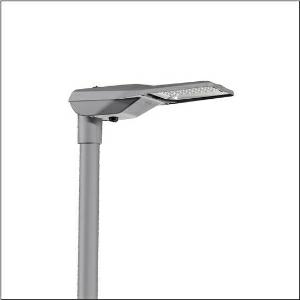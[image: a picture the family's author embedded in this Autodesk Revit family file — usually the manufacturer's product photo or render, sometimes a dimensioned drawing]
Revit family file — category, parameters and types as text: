
# Revit family: streetlight_sl_21_mini___p0_5a_5xe2v33t08gb_dcd0
name_source: partatom
category: Lighting Fixtures
units: mm (PartAtom-declared; Revit-internal decimal feet)

## family parameters
Cut with Voids When Loaded = No
Host = Face
Light Source = No
Part Type = Normal
Room Calculation Point = No
Round Connector Dimension = Use Diameter
Shared = No

## types (1)
- --- (1 x LED, 5840 lm, 40.4 W, 3000K)
    Apparent Load = 40 VA
    CIE Flux Codes = 37 73 96 100 100
    Color Rendering = 70
    Color Temperature = 3000K
    Default Elevation = 1800 mm
    Description = Streetlight SL 21 mini, mast luminaire, primary light control with lens, of PMMA, primary optical cover: cover, of toughened safety glass, transparent, light distribution: P0.5a, light emission: direct distribution, primary light characteristic: asymmetric, installation type: post-top, side-entry, LED, High Power LED, rated luminous flux: 5.840lm, luminous efficacy: 145lm/W, light colour: 730, colour temperature: 3000K, control gear: D4i, control: pre-setting: logarithmic dimming characteristic, flexible luminous flux parameterisation, time-dependent luminous flux control, constant luminous flux control, overheat protection, mains connection: 220..240V, AC, 50/60Hz, start of lifetime: 40W, end of service life: 41W, reduction: 19W, luminaire housing, of diecast aluminium, powder-coated, Siteco® metallic grey (DB 702S), corrosivity category C5 mid according to DIN EN ISO 12944, multi-level sealing system, sealing non-destructively replaceable, inclination adjustable: 0°, 5°, 10°, 15°, please order mast flange separately, length: 628mm, width: 235mm, height: 110mm, mast flange for spigot size: 42mm (side-entry): 5XC10008XM4, 60/48mm (side-entry/post-top): 5XC10108XM2, 76/60mm (side-entry/post-top): 5XC10108XM1, mounting height: 4..8m, Smart Interface below and above, protection rating (complete): IP66, insulation class (complete): insulation class II (safety insulation), certification: CE, ENEC, ENEC+, VDE, impact resistance: IK10, permissible operating ambient temperature for outdoor applications: -40..+50°C, standard-compliant lighting for roads and squares, packaging unit: 1 piece

Light Distribution: P0.5a
    Height = 110 mm
    Lamp = 1 x LED
    Lamp Light Flux = 5840 lm
    Lamp Power = 40.4 W
    Lamp count = 1
    Length = 625 mm
    Luminous efficacy = 145 lm/W
    Manufacturer = Siteco
    ModVariant = No
    Model = 5XE2V33T08GB
    Number of Poles = 1
    OnlyDefault = Yes
    Power Factor = 1
    Product Name = Streetlight SL 21 mini | P0.5a
    Product group = mast luminaire | pylon top
    ProductGroupID = 6100
    Protection Class = Protection class II
    Protection Degree = IP 66
    RLX_Detail_Level = 1
    RLX_Emergency_Light_Flux = 0 lm
    RLX_Emergency_Type = 0
    RLX_Emergency_Type_DB = No
    RlxData = <blob elided: 25889 chars, md5=88b58ec8>
    Socket = socket
    Standby Power = 0 W
    System Light Flux = 5840 lm
    System Power = 40 W
    Type Comments = factory setting: luminous flux: 100 % | dim-lin: 254 | 812 mA
    Type Image = l_1003514.jpg
    URL = http://relux.com
    VarID = @adj_069502
    Voltage = 0 V
    Weight = 0.00 kg
    Width = 234 mm

## geometry (parser evidence)
native form markers: Blend x4, Sweep x11
no freeform markers — native parametric forms only
